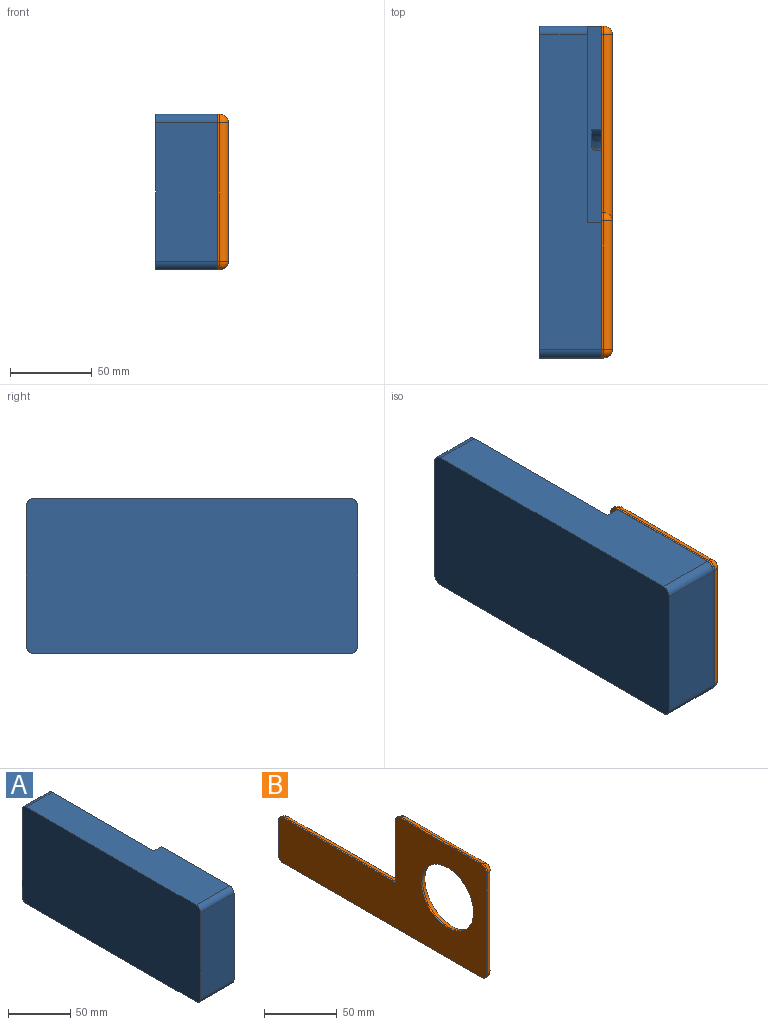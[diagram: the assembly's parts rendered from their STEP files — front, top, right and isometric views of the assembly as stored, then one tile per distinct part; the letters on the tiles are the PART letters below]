
ASSEMBLY  parts=2 mates=1
PART A: 27 faces, bbox 40.4x205.5x97.6 mm
  f0: plane 68.91x43.77mm, normal (1,0,0), area 864.4mm2, adj f1,f9,f11,f18,f22
  f1: plane 121.22x9.46mm, normal (0,0,1), area 994.1mm2, adj f0,f6,f7,f9,f10,f22,f24,f25
  f2: plane 5.38x3.25mm, normal (1,0,0), area 5.5mm2, adj f9,f20,f21
  f3: plane 193.04x38.1mm, normal (0,0,1), area 6327.4mm2, adj f7,f8,f9,f10,f14,f15
  f4: plane 85.09x38.1mm, normal (0,-1,0), area 3241.9mm2, adj f7,f8,f12,f15
  f5: plane 193.04x38.1mm, normal (0,0,-1), area 7354.8mm2, adj f7,f8,f12,f13
  f6: plane 85.09x38.1mm, normal (0,1,0), area 2722.6mm2, adj f1,f7,f8,f10,f13,f14
  f7: plane 203.2x95.25mm, normal (1,0,0), area 7846mm2, adj f1,f3,f4,f5,f6,f9,f11,f12
  f8: plane 203.2x95.25mm, normal (-1,0,0), area 19332.6mm2, adj f3,f4,f5,f6,f12,f13,f14,f15
  f9: plane 65.81x11.2mm, normal (0,1,0), area 488.4mm2, adj f0,f1,f2,f3,f7,f10,f16,f18
  f10: plane 120.65x63.5mm, normal (1,0,0), area 7655.7mm2, adj f1,f3,f6,f9,f14
  f11: sphere r=25.4mm, area 4053.7mm2, adj f0,f7,f17,f23
  f12: cylinder r=5.08mm len=38.1mm, axis (1,0,0), area 304mm2, adj f4,f5,f7,f8
  f13: cylinder r=5.08mm len=38.1mm, axis (-1,0,0), area 304mm2, adj f5,f6,f7,f8
  f14: cylinder r=5.08mm len=29.21mm, axis (1,0,0), area 233.1mm2, adj f3,f6,f8,f10
  f15: cylinder r=5.08mm len=38.1mm, axis (-1,0,0), area 304mm2, adj f3,f4,f7,f8
  f16: extruded ~35.77x25.05mm, area 152.4mm2, adj f7,f9,f17,f21
  f17: cylinder r=25.4mm len=12.84mm, axis (1,0,0), area 92.3mm2, adj f11,f16,f18,f19,f20,f21
  f18: extruded ~27.42x22.93mm, area 119.6mm2, adj f0,f9,f17,f20
  f19: plane 17.84x8.38mm, normal (1,0,0), area 39.6mm2, adj f17,f20,f21
  f20: bspline ~30.59x27.17mm, area 191.2mm2, adj f2,f9,f17,f18,f19,f21
  f21: bspline ~39.48x28.67mm, area 235.2mm2, adj f2,f9,f16,f17,f19,f20
  f22: extruded ~68.19x14.98mm, area 248.5mm2, adj f0,f1,f23,f26
  f23: cylinder r=25.4mm len=12.72mm, axis (1,0,0), area 101.7mm2, adj f11,f22,f24,f25,f26
  f24: extruded ~92.58x15.23mm, area 637.1mm2, adj f1,f7,f23,f25
  f25: plane 93.41x19.63mm, normal (1,0,0), area 397.3mm2, adj f1,f23,f24,f26
  f26: bspline ~73.52x18.49mm, area 415.4mm2, adj f1,f22,f23,f25
PART B: 26 faces, bbox 8.7x203.2x95.3 mm
  f0: plane 85.09x1.27mm, normal (0,-1,0), area 108.1mm2, adj f7,f12,f15,f24
  f1: plane 193.04x1.27mm, normal (0,0,-1), area 245.2mm2, adj f7,f10,f11,f12
  f2: plane 27.94x1.27mm, normal (0,1,0), area 35.5mm2, adj f7,f10,f13,f17
  f3: plane 109.22x1.27mm, normal (0,0,1), area 138.7mm2, adj f4,f7,f13,f19
  f4: plane 52.07x1.27mm, normal (0,1,0), area 66.1mm2, adj f3,f7,f14,f20
  f5: plane 78.74x1.27mm, normal (0,0,1), area 100mm2, adj f7,f14,f15,f22
  f6: plane 193.04x85.09mm, normal (1,0,0), area 6974.9mm2, adj f9,f11,f17,f19,f20,f22,f24
  f7: plane 203.2x95.25mm, normal (-1,0,0), area 10768mm2, adj f0,f1,f2,f3,f4,f5,f8,f10
  f8: cylinder r=25.4mm len=50.8mm, axis (1,0,0), area 202.7mm2, adj f7,f9
  f9: torus R=30.48mm, axis (1,0,0), area 1366mm2, adj f6,f8
  f10: cylinder r=5.08mm len=5.08mm, axis (-1,0,0), area 10.1mm2, adj f1,f2,f7,f16
  f11: cylinder r=5.08mm len=193.04mm, axis (0,-1,0), area 1540.4mm2, adj f1,f6,f16,f25
  f12: cylinder r=5.08mm len=5.08mm, axis (1,0,0), area 10.1mm2, adj f0,f1,f7,f25
  f13: cylinder r=5.08mm len=5.08mm, axis (-1,0,0), area 10.1mm2, adj f2,f3,f7,f18
  f14: cylinder r=5.08mm len=5.08mm, axis (-1,0,0), area 10.1mm2, adj f4,f5,f7,f21
  f15: cylinder r=5.08mm len=5.08mm, axis (-1,0,0), area 10.1mm2, adj f0,f5,f7,f23
  f16: sphere r=5.08mm, area 40.5mm2, adj f10,f11,f17
  f17: cylinder r=5.08mm len=27.94mm, axis (0,0,-1), area 223mm2, adj f2,f6,f16,f18
  f18: sphere r=5.08mm, area 40.5mm2, adj f13,f17,f19
  f19: cylinder r=5.08mm len=114.3mm, axis (0,1,0), area 886.3mm2, adj f3,f6,f18,f20
  f20: cylinder r=5.08mm len=57.15mm, axis (0,0,-1), area 430.2mm2, adj f4,f6,f19,f21
  f21: sphere r=5.08mm, area 40.5mm2, adj f14,f20,f22
  f22: cylinder r=5.08mm len=78.74mm, axis (0,1,0), area 628.3mm2, adj f5,f6,f21,f23
  f23: sphere r=5.08mm, area 40.5mm2, adj f15,f22,f24
  f24: cylinder r=5.08mm len=85.09mm, axis (0,0,1), area 679mm2, adj f0,f6,f23,f25
  f25: sphere r=5.08mm, area 40.5mm2, adj f11,f12,f24
PLACE A t=(-11.22,-46.62,28.07)mm
PLACE B t=(26.88,-46.62,28.07)mm
MATE fastened B.f8 <-> A.f17  axis (-1,0,0) through (26.88,-8.52,78.87)mm
